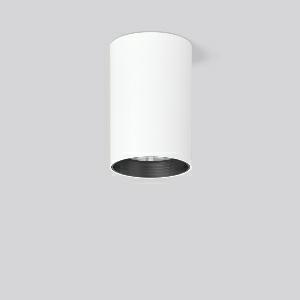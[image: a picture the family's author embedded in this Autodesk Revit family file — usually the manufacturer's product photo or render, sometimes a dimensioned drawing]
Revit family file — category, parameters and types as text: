
# Revit family: heledon_maxi_a_931229_002_8fc8
name_source: partatom
category: Lighting Fixtures
units: mm (PartAtom-declared; Revit-internal decimal feet)

## family parameters
Cut with Voids When Loaded = No
Host = Face
Light Source = No
Part Type = Normal
Room Calculation Point = No
Round Connector Dimension = Use Diameter
Shared = No

## types (1)
- HELEDON maxi A (1 x LED Modul 930, 3600 lm, 3000)
    Apparent Load = 35 VA
    Approval mark = CE
    CIE Flux Codes = 96 100 100 100 100
    Color Rendering = 90
    Color Temperature = 3000
    Default Elevation = 1800 mm
    Description = Series: HELEDON maxi
Cylindrical surface-mounted downlight. Housing: die-cast aluminium, powder-coated. Internal ceiling frame polycarbonate with bayonet mounting. Black plastic ring and recessed LED to prevent glare from the side. Optical assembly with lens made of plastic (polycarbonate) for the best homogeneous light distribution - can be changed without tools. Best colour rendering index Ra>90. Suitable for Ceiling mounting. Easy installation with a separate ceiling frame with bayonet mounting and plug connection. Driver integrated. Connected via plug-in connector. High quality converter without flickering and stroboscopic effect. The following accessories can be mounted without use of tools: interchangeable lenses, decorative glasses, honeycomb louvre, clear and frosted diffusers, white interchangeable plastic ring. 
Colour: traffic white, matt (RAL 9016)
Diameter: 123 mm
Height: 183 mm
Lamp: LED
Socket: without socket
Colour temperature: 3000K
Colour rendering index (CRI): 92
System power: 35 W
Rated luminous flux: 3600 lm
Luminous efficiency: 103 lm/W
Control gear: Regulated power supply
Protection class: I
Type of protection: IP 20
    Height = 183 mm
    Lamp = 1 x LED Modul 930
    Lamp Light Flux = 3600 lm
    Lamp count = 1
    Length = 123 mm
    Lifetime = 50000 h
    Luminous efficacy = 103 lm/W
    Manufacturer = RZB
    ModVariant = No
    Model = 931229.002
    Mounting Place = Ceiling
    Mounting Type = Surface mounted
    Number of Poles = 1
    OnlyDefault = Yes
    Power Factor = 1
    Product Name = HELEDON maxi A
    Product group = Surface mounted downlights
    ProductGroupID = 302
    Protection Class = Protection class I
    Protection Degree = IP 20
    RLX_Detail_Level = 1
    RLX_Emergency_Light_Flux = 0 lm
    RLX_Emergency_Type = 0
    RLX_Emergency_Type_DB = No
    RlxData = <blob elided: 97337 chars, md5=26c96c24>
    Socket = socket
    Standby Power = 0 W
    System Light Flux = 3600 lm
    System Power = 35 W
    Type Comments = Product without accessories
    Type Image = 931193.002.jpg
    URL = http://relux.com
    VarID = ---
    Voltage = 230 V
    Voltage Range = 220-240 V
    Weight = 0.00 kg
    Width = 0 mm  [stored 0 ft]

note: [stored X ft] marks values corroborated as IEEE doubles in the binary element streams (Revit-internal decimal feet)

## geometry (parser evidence)
native form markers: Blend x4, Sweep x11
no freeform markers — native parametric forms only
